# Revit family: Check_Valve-Acorn-Controls-CV_Series
name_source: partatom
category: Pipe Accessories
units: mm (PartAtom-declared; Revit-internal decimal feet)

## family parameters
Always vertical = Yes
Cut with Voids When Loaded = No
OmniClass Number = 23.65.55.14.17
OmniClass Title = Adjusting/Controlling Valves for Liquid Services
Part Type = Normal
Round Connector Dimension = Use Diameter
Shared = Yes
Work Plane-Based = No

## types (5) — shared parameters
0-No Strainer/Filter Included = No
Adapter 0 None = No
Adapter A Sweat = No
Adapter B NPTF = No
Adapter C PEX = No
Adapter D CPVC = No
Adapter E Press Fit = No
Angle Lock = 60.00°
Assembly Code = D2090600
Description = 105MAP-FV Cast Iron Globe Check Style Foot Valve Assembly Sizes: 2" – 24" (50 – 600mm)
F-Strainer/Filter Included = No
Finish = Metal-Acorn-Lead Free
Manufacturer = Acorn Engineering
Material = Metal-Mueller_Steam-Bronze
Pressure Rating = 125 PSI (862 kPa)
Temperature Range = 180°F (82.2°C)
URL = https://www.acorneng.com
Water Supply Pressure = 400psi (27.6bar)

## per-type parameters (varying)
| type | Connection Inlet Description | Connection Outlet Description | Connection Radius | Connection Size | Flow Coefficient Cv | Length A | Length B | Length C |
| CV-1AA0 | 1/2" Sweat Inlet Connection | 1/2" Sweat Outlet Connection | 1/4" | 1/2" | 5.9 | 1 1/8" | 1" | 1 5/8" |
| CV-2BB0 | 3/4" NPTF Inlet Connection | 3/4" NPTF  Outlet Connection | 3/8" | 3/4" | 6.1 | 1 1/8" | 7/8" | 1 5/8" |
| CV-3CC0 | 1" PEX Inlet Connection | 1" PEX  Outlet Connection | 1/2" | 1" | 9.8 | 1 3/8" | 1 1/8" | 1 7/8" |
| CV-4DD0 | 1 1/4" CPVC Inlet Connection | 1 1/4" CPVC  Outlet Connection | 5/8" | 1 1/4" | 21.0 | 1 7/8" | 1 1/4" | 2 3/8" |
| CV-5EE0 | 1 1/2" Press Fit Inlet Connection | 1 1/2" Press Fit Outlet Connection | 3/4" | 1 1/2" | 25.3 | 1 7/8" | 2" | 2 7/8" |

note: column(s) folded — value = type name in every type: Model

## geometry (parser evidence)
native form markers: Sweep x3
no freeform markers — native parametric forms only
